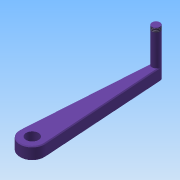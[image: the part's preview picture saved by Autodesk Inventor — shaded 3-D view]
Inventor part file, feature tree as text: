
AUTODESK INVENTOR PART (.ipt)
format: ipt  version: 2015 (Build 190159000, 159)  size: 111,616 bytes
history: native  units: mm
features: extrude x3, chamfer x3, sketch x3, thread x1
ambient origin geometry x8: Origin, YZ Plane, XZ Plane, XY Plane, X Axis, Y Axis, Z Axis, Center Point
bodies: 实体1 (feature_tree)
feature tree (10):
  extrude  "拉伸1"  Depth=10.0mm
  extrude  "拉伸2"  Depth=15.0mm TaperAngle=0.0deg
  extrude  "拉伸3"  Depth=15.0mm
  thread  "螺纹1"  [1 undecoded]
  chamfer  "倒角1"  Distance=10.0mm
  chamfer  "倒角2"  Distance=42.5mm
  chamfer  "倒角3"  Distance=5.0mm
  sketch  "草图1"  dims[d0=30.0mm d1=10.0mm]
  sketch  "草图2"  dims[d2=150.0mm d3=15.0mm d4=0.0mm]
  sketch  "草图3"  dims[d5=15.0mm d6=15.0mm d7=0.0mm d8=10.0mm d9=42.5mm d10=0.0mm d11=5.0mm d12=0.0mm d13=0.25mm d14=2.0mm d15=45.0deg d16=1.0mm d17=2.0mm d18=45.0deg d19=0.25mm d20=2.0mm d21=45.0deg]
note: 1 required parameter value undecoded (feature->parameter linkage not recoverable at this tier; creation-order binding heuristic only, values carry confidence <= 0.55)
